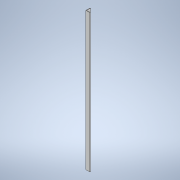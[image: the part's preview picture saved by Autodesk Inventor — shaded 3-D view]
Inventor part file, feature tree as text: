
AUTODESK INVENTOR PART (.ipt)
format: ipt  version: 2021 (Build 250183000, 183)  size: 99,840 bytes
history: native  units: in
note: dims shown in document units (in); Inventor stores cm internally (conversion verified against a paired STEP export)
features: extrude x1, sketch x1
ambient origin geometry x8: Origin, YZ Plane, XZ Plane, XY Plane, X Axis, Y Axis, Z Axis, Center Point
bodies: Solid1 (feature_tree)
feature tree (2):
  extrude  "Extrusion1"  Depth=0.1181in
  sketch  "Sketch1"  dims[d0=0.1181in d1=0.1181in d2=1.1811in d3=1.1811in d4=39.3701in d5=0.0in]
